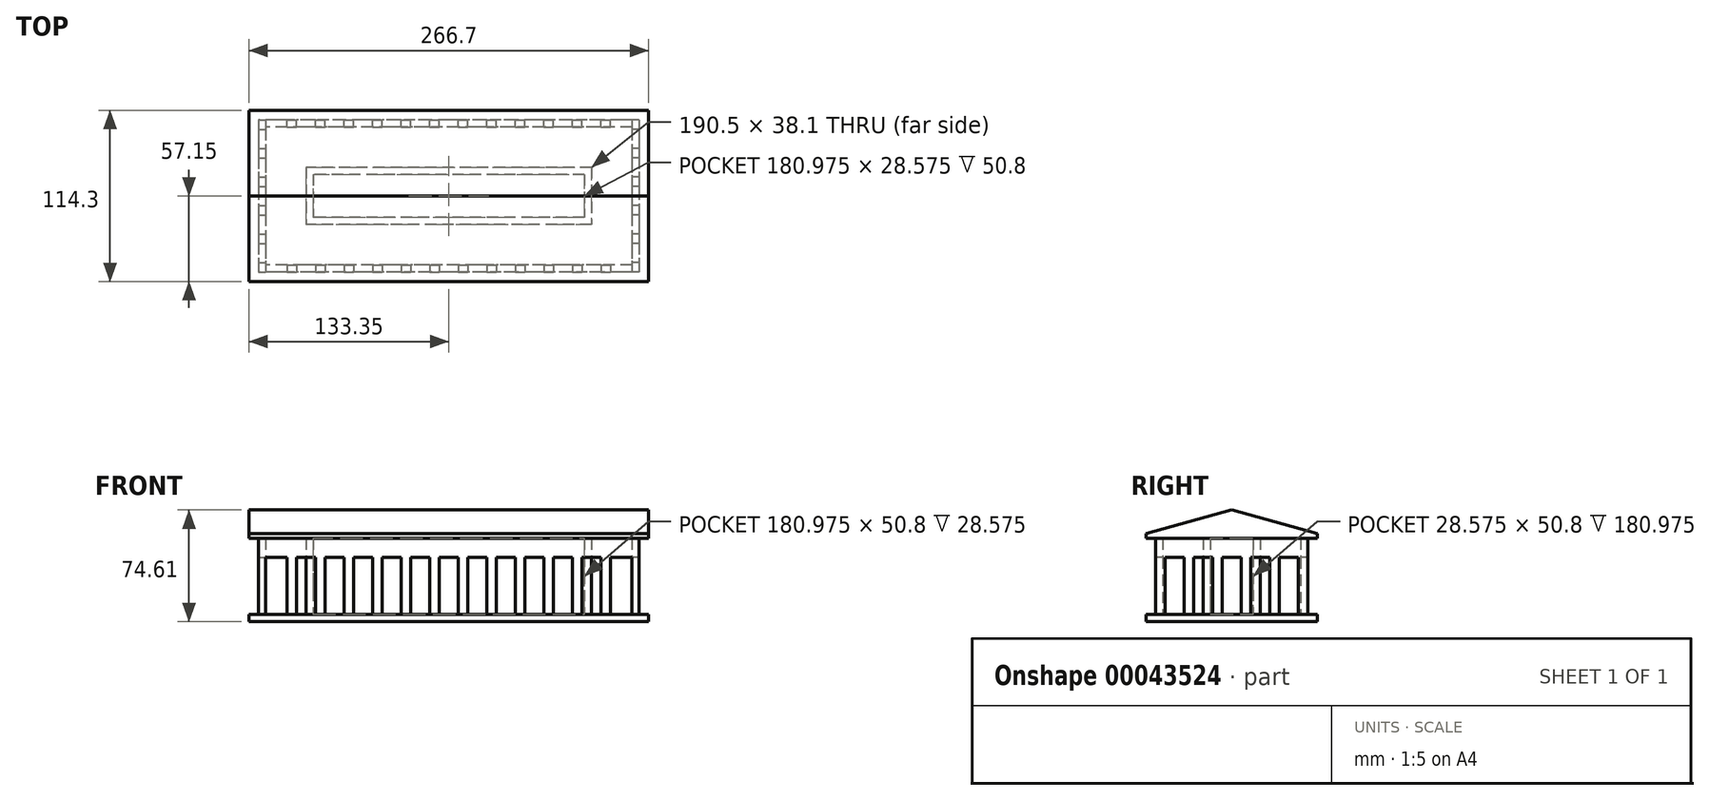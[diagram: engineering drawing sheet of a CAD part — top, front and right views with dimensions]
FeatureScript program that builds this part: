
annotation { "Feature Type Name" : "Feature", "Feature Type Description" : "" }
export const myFeature = defineFeature(function(context is Context, id is Id, definition is map)
    precondition{}
    {
        {
            var Q0;
            Q0=qCreatedBy(makeId("Top.planeOp"),FACE);
            var sketch = newSketch(context, id + "F0", { "sketchPlane" : qUnion([Q0])});
            skLineSegment(sketch, "E0.bottom", {"start": v(0, 0) * mm, "end": v(-266.7, 0) * mm});
            skLineSegment(sketch, "E0.top", {"start": v(0, -114.3) * mm, "end": v(-266.7, -114.3) * mm});
            skLineSegment(sketch, "E0.left", {"start": v(0, 0) * mm, "end": v(0, -114.3) * mm});
            skLineSegment(sketch, "E0.right", {"start": v(-266.7, 0) * mm, "end": v(-266.7, -114.3) * mm});
            skSolve(sketch);
        }
        {
            var Q0;
            Q0 = qSketchRegion(id + "F0", true);
            var Q1;
            Q1 = qSketchRegion(id + "FEWzJ1hWetXT4Pq_1", true);
            extrude(context, id + "F1", {"entities" : qUnion([Q0, Q1]), "depth" : 4.78 * mm});
        }
        {
            var Q0;
            Q0=makeQuery(id+"F1.opExtrude","CAP_FACE",FACE,{"disambiguationData":[OSD([sQuery(id+"F0.wireOp",EDGE,"E0.bottom"),sQuery(id+"F0.wireOp",EDGE,"E0.top"),sQuery(id+"F0.wireOp",EDGE,"E0.left"),sQuery(id+"F0.wireOp",EDGE,"E0.right")])],"isStart":false});
            var sketch = newSketch(context, id + "F2", { "sketchPlane" : qUnion([Q0])});
            skLineSegment(sketch, "E1.bottom", {"start": v(-260.35, -101.6) * mm, "end": v(-255.59, -101.6) * mm});
            skLineSegment(sketch, "E1.top", {"start": v(-260.35, -107.95) * mm, "end": v(-255.59, -107.95) * mm});
            skLineSegment(sketch, "E1.left", {"start": v(-260.35, -101.6) * mm, "end": v(-260.35, -107.95) * mm});
            skLineSegment(sketch, "E1.right", {"start": v(-255.59, -101.6) * mm, "end": v(-255.59, -107.95) * mm});
            skLineSegment(sketch, "E2.0.1.0", {"start": v(-260.35, -88.9) * mm, "end": v(-255.59, -88.9) * mm});
            skLineSegment(sketch, "E2.0.1.1", {"start": v(-255.59, -82.55) * mm, "end": v(-255.59, -88.9) * mm});
            skLineSegment(sketch, "E2.0.1.2", {"start": v(-260.35, -82.55) * mm, "end": v(-260.35, -88.9) * mm});
            skLineSegment(sketch, "E2.0.1.3", {"start": v(-260.35, -82.55) * mm, "end": v(-255.59, -82.55) * mm});
            skLineSegment(sketch, "E2.0.2.0", {"start": v(-260.35, -69.85) * mm, "end": v(-255.59, -69.85) * mm});
            skLineSegment(sketch, "E2.0.2.1", {"start": v(-255.59, -63.5) * mm, "end": v(-255.59, -69.85) * mm});
            skLineSegment(sketch, "E2.0.2.2", {"start": v(-260.35, -63.5) * mm, "end": v(-260.35, -69.85) * mm});
            skLineSegment(sketch, "E2.0.2.3", {"start": v(-260.35, -63.5) * mm, "end": v(-255.59, -63.5) * mm});
            skLineSegment(sketch, "E2.0.3.0", {"start": v(-260.35, -50.8) * mm, "end": v(-255.59, -50.8) * mm});
            skLineSegment(sketch, "E2.0.3.1", {"start": v(-255.59, -44.45) * mm, "end": v(-255.59, -50.8) * mm});
            skLineSegment(sketch, "E2.0.3.2", {"start": v(-260.35, -44.45) * mm, "end": v(-260.35, -50.8) * mm});
            skLineSegment(sketch, "E2.0.3.3", {"start": v(-260.35, -44.45) * mm, "end": v(-255.59, -44.45) * mm});
            skLineSegment(sketch, "E2.0.4.0", {"start": v(-260.35, -31.75) * mm, "end": v(-255.59, -31.75) * mm});
            skLineSegment(sketch, "E2.0.4.1", {"start": v(-255.59, -25.4) * mm, "end": v(-255.59, -31.75) * mm});
            skLineSegment(sketch, "E2.0.4.2", {"start": v(-260.35, -25.4) * mm, "end": v(-260.35, -31.75) * mm});
            skLineSegment(sketch, "E2.0.4.3", {"start": v(-260.35, -25.4) * mm, "end": v(-255.59, -25.4) * mm});
            skLineSegment(sketch, "E2.0.5.0", {"start": v(-260.35, -12.7) * mm, "end": v(-255.59, -12.7) * mm});
            skLineSegment(sketch, "E2.0.5.1", {"start": v(-255.59, -6.35) * mm, "end": v(-255.59, -12.7) * mm});
            skLineSegment(sketch, "E2.0.5.2", {"start": v(-260.35, -6.35) * mm, "end": v(-260.35, -12.7) * mm});
            skLineSegment(sketch, "E2.0.5.3", {"start": v(-260.35, -6.35) * mm, "end": v(-255.59, -6.35) * mm});
            skLineSegment(sketch, "E2.direction1", {"start": v(-260.35, -107.95) * mm, "end": v(-251.94, -107.95) * mm, "construction": true});
            skLineSegment(sketch, "E2.direction2", {"start": v(-260.35, -107.95) * mm, "end": v(-260.35, -88.9) * mm, "construction": true});
            skLineSegment(sketch, "E3.bottom", {"start": v(-241.3, -103.19) * mm, "end": v(-234.95, -103.19) * mm});
            skLineSegment(sketch, "E3.top", {"start": v(-241.3, -107.95) * mm, "end": v(-234.95, -107.95) * mm});
            skLineSegment(sketch, "E3.left", {"start": v(-241.3, -103.19) * mm, "end": v(-241.3, -107.95) * mm});
            skLineSegment(sketch, "E3.right", {"start": v(-234.95, -103.19) * mm, "end": v(-234.95, -107.95) * mm});
            skLineSegment(sketch, "E4.1.0.0", {"start": v(-222.25, -107.95) * mm, "end": v(-215.9, -107.95) * mm});
            skLineSegment(sketch, "E4.1.0.1", {"start": v(-215.9, -103.19) * mm, "end": v(-215.9, -107.95) * mm});
            skLineSegment(sketch, "E4.1.0.2", {"start": v(-222.25, -103.19) * mm, "end": v(-222.25, -107.95) * mm});
            skLineSegment(sketch, "E4.1.0.3", {"start": v(-222.25, -103.19) * mm, "end": v(-215.9, -103.19) * mm});
            skLineSegment(sketch, "E4.2.0.0", {"start": v(-203.2, -107.95) * mm, "end": v(-196.85, -107.95) * mm});
            skLineSegment(sketch, "E4.2.0.1", {"start": v(-196.85, -103.19) * mm, "end": v(-196.85, -107.95) * mm});
            skLineSegment(sketch, "E4.2.0.2", {"start": v(-203.2, -103.19) * mm, "end": v(-203.2, -107.95) * mm});
            skLineSegment(sketch, "E4.2.0.3", {"start": v(-203.2, -103.19) * mm, "end": v(-196.85, -103.19) * mm});
            skLineSegment(sketch, "E4.3.0.0", {"start": v(-184.15, -107.95) * mm, "end": v(-177.8, -107.95) * mm});
            skLineSegment(sketch, "E4.3.0.1", {"start": v(-177.8, -103.19) * mm, "end": v(-177.8, -107.95) * mm});
            skLineSegment(sketch, "E4.3.0.2", {"start": v(-184.15, -103.19) * mm, "end": v(-184.15, -107.95) * mm});
            skLineSegment(sketch, "E4.3.0.3", {"start": v(-184.15, -103.19) * mm, "end": v(-177.8, -103.19) * mm});
            skLineSegment(sketch, "E4.4.0.0", {"start": v(-165.1, -107.95) * mm, "end": v(-158.75, -107.95) * mm});
            skLineSegment(sketch, "E4.4.0.1", {"start": v(-158.75, -103.19) * mm, "end": v(-158.75, -107.95) * mm});
            skLineSegment(sketch, "E4.4.0.2", {"start": v(-165.1, -103.19) * mm, "end": v(-165.1, -107.95) * mm});
            skLineSegment(sketch, "E4.4.0.3", {"start": v(-165.1, -103.19) * mm, "end": v(-158.75, -103.19) * mm});
            skLineSegment(sketch, "E4.5.0.0", {"start": v(-146.05, -107.95) * mm, "end": v(-139.7, -107.95) * mm});
            skLineSegment(sketch, "E4.5.0.1", {"start": v(-139.7, -103.19) * mm, "end": v(-139.7, -107.95) * mm});
            skLineSegment(sketch, "E4.5.0.2", {"start": v(-146.05, -103.19) * mm, "end": v(-146.05, -107.95) * mm});
            skLineSegment(sketch, "E4.5.0.3", {"start": v(-146.05, -103.19) * mm, "end": v(-139.7, -103.19) * mm});
            skLineSegment(sketch, "E4.6.0.0", {"start": v(-127, -107.95) * mm, "end": v(-120.65, -107.95) * mm});
            skLineSegment(sketch, "E4.6.0.1", {"start": v(-120.65, -103.19) * mm, "end": v(-120.65, -107.95) * mm});
            skLineSegment(sketch, "E4.6.0.2", {"start": v(-127, -103.19) * mm, "end": v(-127, -107.95) * mm});
            skLineSegment(sketch, "E4.6.0.3", {"start": v(-127, -103.19) * mm, "end": v(-120.65, -103.19) * mm});
            skLineSegment(sketch, "E4.7.0.0", {"start": v(-107.95, -107.95) * mm, "end": v(-101.6, -107.95) * mm});
            skLineSegment(sketch, "E4.7.0.1", {"start": v(-101.6, -103.19) * mm, "end": v(-101.6, -107.95) * mm});
            skLineSegment(sketch, "E4.7.0.2", {"start": v(-107.95, -103.19) * mm, "end": v(-107.95, -107.95) * mm});
            skLineSegment(sketch, "E4.7.0.3", {"start": v(-107.95, -103.19) * mm, "end": v(-101.6, -103.19) * mm});
            skLineSegment(sketch, "E4.8.0.0", {"start": v(-88.9, -107.95) * mm, "end": v(-82.55, -107.95) * mm});
            skLineSegment(sketch, "E4.8.0.1", {"start": v(-82.55, -103.19) * mm, "end": v(-82.55, -107.95) * mm});
            skLineSegment(sketch, "E4.8.0.2", {"start": v(-88.9, -103.19) * mm, "end": v(-88.9, -107.95) * mm});
            skLineSegment(sketch, "E4.8.0.3", {"start": v(-88.9, -103.19) * mm, "end": v(-82.55, -103.19) * mm});
            skLineSegment(sketch, "E4.9.0.0", {"start": v(-69.85, -107.95) * mm, "end": v(-63.5, -107.95) * mm});
            skLineSegment(sketch, "E4.9.0.1", {"start": v(-63.5, -103.19) * mm, "end": v(-63.5, -107.95) * mm});
            skLineSegment(sketch, "E4.9.0.2", {"start": v(-69.85, -103.19) * mm, "end": v(-69.85, -107.95) * mm});
            skLineSegment(sketch, "E4.9.0.3", {"start": v(-69.85, -103.19) * mm, "end": v(-63.5, -103.19) * mm});
            skLineSegment(sketch, "E4.10.0.0", {"start": v(-50.8, -107.95) * mm, "end": v(-44.45, -107.95) * mm});
            skLineSegment(sketch, "E4.10.0.1", {"start": v(-44.45, -103.19) * mm, "end": v(-44.45, -107.95) * mm});
            skLineSegment(sketch, "E4.10.0.2", {"start": v(-50.8, -103.19) * mm, "end": v(-50.8, -107.95) * mm});
            skLineSegment(sketch, "E4.10.0.3", {"start": v(-50.8, -103.19) * mm, "end": v(-44.45, -103.19) * mm});
            skLineSegment(sketch, "E4.11.0.0", {"start": v(-31.75, -107.95) * mm, "end": v(-25.4, -107.95) * mm});
            skLineSegment(sketch, "E4.11.0.1", {"start": v(-25.4, -103.19) * mm, "end": v(-25.4, -107.95) * mm});
            skLineSegment(sketch, "E4.11.0.2", {"start": v(-31.75, -103.19) * mm, "end": v(-31.75, -107.95) * mm});
            skLineSegment(sketch, "E4.11.0.3", {"start": v(-31.75, -103.19) * mm, "end": v(-25.4, -103.19) * mm});
            skLineSegment(sketch, "E4.direction1", {"start": v(-241.3, -107.95) * mm, "end": v(-222.25, -107.95) * mm, "construction": true});
            skLineSegment(sketch, "E5.MirrorCS", {"start": v(-6.35, -107.95) * mm, "end": v(-11.11, -107.95) * mm});
            skLineSegment(sketch, "E6.MirrorCS", {"start": v(-6.35, -82.55) * mm, "end": v(-6.35, -88.9) * mm});
            skLineSegment(sketch, "E7.MirrorCS", {"start": v(-6.35, -82.55) * mm, "end": v(-11.11, -82.55) * mm});
            skLineSegment(sketch, "E8.MirrorCS", {"start": v(-6.35, -12.7) * mm, "end": v(-11.11, -12.7) * mm});
            skLineSegment(sketch, "E9.MirrorCS", {"start": v(-11.11, -6.35) * mm, "end": v(-11.11, -12.7) * mm});
            skLineSegment(sketch, "E10.MirrorCS", {"start": v(-6.35, -6.35) * mm, "end": v(-6.35, -12.7) * mm});
            skLineSegment(sketch, "E11.MirrorCS", {"start": v(-6.35, -6.35) * mm, "end": v(-11.11, -6.35) * mm});
            skLineSegment(sketch, "E12.MirrorCS", {"start": v(-6.35, -31.75) * mm, "end": v(-11.11, -31.75) * mm});
            skLineSegment(sketch, "E13.MirrorCS", {"start": v(-11.11, -25.4) * mm, "end": v(-11.11, -31.75) * mm});
            skLineSegment(sketch, "E14.MirrorCS", {"start": v(-11.11, -44.45) * mm, "end": v(-11.11, -50.8) * mm});
            skLineSegment(sketch, "E15.MirrorCS", {"start": v(-6.35, -44.45) * mm, "end": v(-6.35, -50.8) * mm});
            skLineSegment(sketch, "E16.MirrorCS", {"start": v(-6.35, -44.45) * mm, "end": v(-11.11, -44.45) * mm});
            skLineSegment(sketch, "E17.MirrorCS", {"start": v(-6.35, -25.4) * mm, "end": v(-6.35, -31.75) * mm});
            skLineSegment(sketch, "E18.MirrorCS", {"start": v(-11.11, -63.5) * mm, "end": v(-11.11, -69.85) * mm});
            skLineSegment(sketch, "E19.MirrorCS", {"start": v(-6.35, -101.6) * mm, "end": v(-11.11, -101.6) * mm});
            skLineSegment(sketch, "E20.MirrorCS", {"start": v(-6.35, -101.6) * mm, "end": v(-6.35, -107.95) * mm});
            skLineSegment(sketch, "E21.MirrorCS", {"start": v(-6.35, -63.5) * mm, "end": v(-6.35, -69.85) * mm});
            skLineSegment(sketch, "E22.MirrorCS", {"start": v(-6.35, -69.85) * mm, "end": v(-11.11, -69.85) * mm});
            skLineSegment(sketch, "E23.MirrorCS", {"start": v(-11.11, -101.6) * mm, "end": v(-11.11, -107.95) * mm});
            skLineSegment(sketch, "E24.MirrorCS", {"start": v(-6.35, -88.9) * mm, "end": v(-11.11, -88.9) * mm});
            skLineSegment(sketch, "E25.MirrorCS", {"start": v(-6.35, -63.5) * mm, "end": v(-11.11, -63.5) * mm});
            skLineSegment(sketch, "E26.MirrorCS", {"start": v(-6.35, -50.8) * mm, "end": v(-11.11, -50.8) * mm});
            skLineSegment(sketch, "E27.MirrorCS", {"start": v(-11.11, -82.55) * mm, "end": v(-11.11, -88.9) * mm});
            skLineSegment(sketch, "E28.MirrorCS", {"start": v(-6.35, -25.4) * mm, "end": v(-11.11, -25.4) * mm});
            skLineSegment(sketch, "E29.direction1", {"start": v(0, 0) * mm, "end": v(25.4, 0) * mm, "construction": true});
            skLineSegment(sketch, "E30.MirrorCS", {"start": v(-120.65, -11.11) * mm, "end": v(-120.65, -6.35) * mm});
            skLineSegment(sketch, "E31.MirrorCS", {"start": v(-203.2, -6.35) * mm, "end": v(-196.85, -6.35) * mm});
            skLineSegment(sketch, "E32.MirrorCS", {"start": v(-184.15, -11.11) * mm, "end": v(-177.8, -11.11) * mm});
            skLineSegment(sketch, "E33.MirrorCS", {"start": v(-31.75, -11.11) * mm, "end": v(-25.4, -11.11) * mm});
            skLineSegment(sketch, "E34.MirrorCS", {"start": v(-203.2, -11.11) * mm, "end": v(-203.2, -6.35) * mm});
            skLineSegment(sketch, "E35.MirrorCS", {"start": v(-177.8, -11.11) * mm, "end": v(-177.8, -6.35) * mm});
            skLineSegment(sketch, "E36.MirrorCS", {"start": v(-196.85, -11.11) * mm, "end": v(-196.85, -6.35) * mm});
            skLineSegment(sketch, "E37.MirrorCS", {"start": v(-165.1, -6.35) * mm, "end": v(-158.75, -6.35) * mm});
            skLineSegment(sketch, "E38.MirrorCS", {"start": v(-25.4, -11.11) * mm, "end": v(-25.4, -6.35) * mm});
            skLineSegment(sketch, "E39.MirrorCS", {"start": v(-241.3, -11.11) * mm, "end": v(-234.95, -11.11) * mm});
            skLineSegment(sketch, "E40.MirrorCS", {"start": v(-88.9, -6.35) * mm, "end": v(-82.55, -6.35) * mm});
            skLineSegment(sketch, "E41.MirrorCS", {"start": v(-165.1, -11.11) * mm, "end": v(-158.75, -11.11) * mm});
            skLineSegment(sketch, "E42.MirrorCS", {"start": v(-146.05, -11.11) * mm, "end": v(-146.05, -6.35) * mm});
            skLineSegment(sketch, "E43.MirrorCS", {"start": v(-69.85, -11.11) * mm, "end": v(-69.85, -6.35) * mm});
            skLineSegment(sketch, "E44.MirrorCS", {"start": v(-88.9, -11.11) * mm, "end": v(-88.9, -6.35) * mm});
            skLineSegment(sketch, "E45.MirrorCS", {"start": v(-234.95, -11.11) * mm, "end": v(-234.95, -6.35) * mm});
            skLineSegment(sketch, "E46.MirrorCS", {"start": v(-165.1, -11.11) * mm, "end": v(-165.1, -6.35) * mm});
            skLineSegment(sketch, "E47.MirrorCS", {"start": v(-241.3, -11.11) * mm, "end": v(-241.3, -6.35) * mm});
            skLineSegment(sketch, "E48.MirrorCS", {"start": v(-222.25, -6.35) * mm, "end": v(-215.9, -6.35) * mm});
            skLineSegment(sketch, "E49.MirrorCS", {"start": v(-203.2, -11.11) * mm, "end": v(-196.85, -11.11) * mm});
            skLineSegment(sketch, "E50.MirrorCS", {"start": v(-146.05, -11.11) * mm, "end": v(-139.7, -11.11) * mm});
            skLineSegment(sketch, "E51.MirrorCS", {"start": v(-107.95, -6.35) * mm, "end": v(-101.6, -6.35) * mm});
            skLineSegment(sketch, "E52.MirrorCS", {"start": v(-63.5, -11.11) * mm, "end": v(-63.5, -6.35) * mm});
            skLineSegment(sketch, "E53.MirrorCS", {"start": v(-127, -6.35) * mm, "end": v(-120.65, -6.35) * mm});
            skLineSegment(sketch, "E54.MirrorCS", {"start": v(-69.85, -11.11) * mm, "end": v(-63.5, -11.11) * mm});
            skLineSegment(sketch, "E55.MirrorCS", {"start": v(-50.8, -6.35) * mm, "end": v(-44.45, -6.35) * mm});
            skLineSegment(sketch, "E56.MirrorCS", {"start": v(-184.15, -11.11) * mm, "end": v(-184.15, -6.35) * mm});
            skLineSegment(sketch, "E57.MirrorCS", {"start": v(-107.95, -11.11) * mm, "end": v(-101.6, -11.11) * mm});
            skLineSegment(sketch, "E58.MirrorCS", {"start": v(-241.3, -6.35) * mm, "end": v(-234.95, -6.35) * mm});
            skLineSegment(sketch, "E59.MirrorCS", {"start": v(-50.8, -11.11) * mm, "end": v(-50.8, -6.35) * mm});
            skLineSegment(sketch, "E60.MirrorCS", {"start": v(-107.95, -11.11) * mm, "end": v(-107.95, -6.35) * mm});
            skLineSegment(sketch, "E61.MirrorCS", {"start": v(-44.45, -11.11) * mm, "end": v(-44.45, -6.35) * mm});
            skLineSegment(sketch, "E62.MirrorCS", {"start": v(-222.25, -11.11) * mm, "end": v(-222.25, -6.35) * mm});
            skLineSegment(sketch, "E63.MirrorCS", {"start": v(-82.55, -11.11) * mm, "end": v(-82.55, -6.35) * mm});
            skLineSegment(sketch, "E64.MirrorCS", {"start": v(-101.6, -11.11) * mm, "end": v(-101.6, -6.35) * mm});
            skLineSegment(sketch, "E65.MirrorCS", {"start": v(-31.75, -11.11) * mm, "end": v(-31.75, -6.35) * mm});
            skLineSegment(sketch, "E66.MirrorCS", {"start": v(-88.9, -11.11) * mm, "end": v(-82.55, -11.11) * mm});
            skLineSegment(sketch, "E67.MirrorCS", {"start": v(-139.7, -11.11) * mm, "end": v(-139.7, -6.35) * mm});
            skLineSegment(sketch, "E68.MirrorCS", {"start": v(-31.75, -6.35) * mm, "end": v(-25.4, -6.35) * mm});
            skLineSegment(sketch, "E69.MirrorCS", {"start": v(-50.8, -11.11) * mm, "end": v(-44.45, -11.11) * mm});
            skLineSegment(sketch, "E70.MirrorCS", {"start": v(-69.85, -6.35) * mm, "end": v(-63.5, -6.35) * mm});
            skLineSegment(sketch, "E71.MirrorCS", {"start": v(-127, -11.11) * mm, "end": v(-120.65, -11.11) * mm});
            skLineSegment(sketch, "E72.MirrorCS", {"start": v(-127, -11.11) * mm, "end": v(-127, -6.35) * mm});
            skLineSegment(sketch, "E73.MirrorCS", {"start": v(-222.25, -11.11) * mm, "end": v(-215.9, -11.11) * mm});
            skLineSegment(sketch, "E74.MirrorCS", {"start": v(-215.9, -11.11) * mm, "end": v(-215.9, -6.35) * mm});
            skLineSegment(sketch, "E75.MirrorCS", {"start": v(-146.05, -6.35) * mm, "end": v(-139.7, -6.35) * mm});
            skLineSegment(sketch, "E76.MirrorCS", {"start": v(-158.75, -11.11) * mm, "end": v(-158.75, -6.35) * mm});
            skLineSegment(sketch, "E77.MirrorCS", {"start": v(-184.15, -6.35) * mm, "end": v(-177.8, -6.35) * mm});
            skSolve(sketch);
        }
        {
            var Q0;
            Q0 = qSketchRegion(id + "F2", true);
            var Q1;
            Q1 = qSketchRegion(id + "F6IGndgWyHRMqrs_1", true);
            extrude(context, id + "F3", {"entities" : qUnion([Q0, Q1]), "operationType" : NewBodyOperationType.ADD, "depth" : 38.1 * mm});
        }
        {
            var Q0;
            Q0=makeQuery(id+"F1.opExtrude","CAP_FACE",FACE,{"disambiguationData":[OSD([sQuery(id+"F0.wireOp",EDGE,"E0.bottom"),sQuery(id+"F0.wireOp",EDGE,"E0.top"),sQuery(id+"F0.wireOp",EDGE,"E0.left"),sQuery(id+"F0.wireOp",EDGE,"E0.right")])],"isStart":false});
            var sketch = newSketch(context, id + "F4", { "sketchPlane" : qUnion([Q0])});
            skLineSegment(sketch, "E78.0", {"start": v(-38.1, -38.1) * mm, "end": v(-228.6, -38.1) * mm});
            skLineSegment(sketch, "E78.1", {"start": v(-38.1, -38.1) * mm, "end": v(-38.1, -76.2) * mm});
            skLineSegment(sketch, "E78.2", {"start": v(-38.1, -76.2) * mm, "end": v(-228.6, -76.2) * mm});
            skLineSegment(sketch, "E78.3", {"start": v(-228.6, -38.1) * mm, "end": v(-228.6, -76.2) * mm});
            skLineSegment(sketch, "E79.0", {"start": v(-42.86, -42.86) * mm, "end": v(-223.84, -42.86) * mm});
            skLineSegment(sketch, "E79.1", {"start": v(-42.86, -42.86) * mm, "end": v(-42.86, -71.44) * mm});
            skLineSegment(sketch, "E79.2", {"start": v(-42.86, -71.44) * mm, "end": v(-223.84, -71.44) * mm});
            skLineSegment(sketch, "E79.3", {"start": v(-223.84, -42.86) * mm, "end": v(-223.84, -71.44) * mm});
            skLineSegment(sketch, "E80.0", {"start": v(-6.35, -107.95) * mm, "end": v(-6.35, -6.35) * mm});
            skLineSegment(sketch, "E80.1", {"start": v(-260.35, -107.95) * mm, "end": v(-6.35, -107.95) * mm});
            skLineSegment(sketch, "E80.2", {"start": v(-260.35, -6.35) * mm, "end": v(-260.35, -107.95) * mm});
            skLineSegment(sketch, "E80.3", {"start": v(-6.35, -6.35) * mm, "end": v(-260.35, -6.35) * mm});
            skLineSegment(sketch, "E81.0", {"start": v(0, -107.95) * mm, "end": v(0, -6.35) * mm});
            skSolve(sketch);
        }
        {
            var Q0;
            Q0=makeQuery(id+"F4.imprint","IMPRINT",FACE,{"disambiguationData":[TD([[makeQuery(id+"F4.imprint","IMPRINT",EDGE,{"derivedFrom":sQuery(id+"F4.wireOp",EDGE,"E78.0")}),1.0]])]});
            extrude(context, id + "F5", {"entities" : qUnion([Q0]), "operationType" : NewBodyOperationType.ADD, "depth" : 50.8 * mm});
        }
        {
            var Q0;
            Q0=makeQuery(id+"F3.opExtrude","CAP_FACE",FACE,{"disambiguationData":[OSD([sQuery(id+"F2.wireOp",EDGE,"E48.MirrorCS"),sQuery(id+"F2.wireOp",EDGE,"E62.MirrorCS"),sQuery(id+"F2.wireOp",EDGE,"E73.MirrorCS"),sQuery(id+"F2.wireOp",EDGE,"E74.MirrorCS")])],"isStart":false});
            var sketch = newSketch(context, id + "F6", { "sketchPlane" : qUnion([Q0])});
            skLineSegment(sketch, "E82.bottom", {"start": v(-6.35, -6.35) * mm, "end": v(-260.35, -6.35) * mm});
            skLineSegment(sketch, "E82.top", {"start": v(-6.35, -107.95) * mm, "end": v(-260.35, -107.95) * mm});
            skLineSegment(sketch, "E82.left", {"start": v(-6.35, -6.35) * mm, "end": v(-6.35, -107.95) * mm});
            skLineSegment(sketch, "E82.right", {"start": v(-260.35, -6.35) * mm, "end": v(-260.35, -107.95) * mm});
            skLineSegment(sketch, "E83.0", {"start": v(-11.11, -11.11) * mm, "end": v(-255.59, -11.11) * mm});
            skLineSegment(sketch, "E83.1", {"start": v(-11.11, -11.11) * mm, "end": v(-11.11, -103.19) * mm});
            skLineSegment(sketch, "E83.2", {"start": v(-11.11, -103.19) * mm, "end": v(-255.59, -103.19) * mm});
            skLineSegment(sketch, "E83.3", {"start": v(-255.59, -11.11) * mm, "end": v(-255.59, -103.19) * mm});
            skLineSegment(sketch, "E84.0", {"start": v(-6.35, -107.95) * mm, "end": v(-6.35, -6.35) * mm});
            skLineSegment(sketch, "E84.1", {"start": v(-260.35, -107.95) * mm, "end": v(-6.35, -107.95) * mm});
            skSolve(sketch);
        }
        {
            var Q0;
            Q0 = qSketchRegion(id + "F6", true);
            extrude(context, id + "F7", {"entities" : qUnion([Q0]), "operationType" : NewBodyOperationType.ADD, "depth" : 12.7 * mm});
        }
        {
            var Q0;
            Q0=makeQuery(id+"F1.opExtrude","SWEPT_FACE",FACE,{"disambiguationData":[OSD([sQuery(id+"F0.wireOp",EDGE,"E0.right")])]});
            var sketch = newSketch(context, id + "F8", { "sketchPlane" : qUnion([Q0])});
            skLineSegment(sketch, "E85.0.0", {"start": v(101.6, 4.78) * mm, "end": v(107.95, 4.78) * mm});
            skLineSegment(sketch, "E85.0.1", {"start": v(107.95, 4.78) * mm, "end": v(107.95, 55.58) * mm});
            skLineSegment(sketch, "E85.0.2", {"start": v(107.95, 55.58) * mm, "end": v(6.35, 55.58) * mm});
            skLineSegment(sketch, "E85.0.3", {"start": v(6.35, 55.58) * mm, "end": v(6.35, 4.78) * mm});
            skLineSegment(sketch, "E85.0.4", {"start": v(6.35, 4.78) * mm, "end": v(12.7, 4.78) * mm});
            skLineSegment(sketch, "E85.0.5", {"start": v(12.7, 4.78) * mm, "end": v(12.7, 42.88) * mm});
            skLineSegment(sketch, "E85.0.6", {"start": v(12.7, 42.88) * mm, "end": v(25.4, 42.88) * mm});
            skLineSegment(sketch, "E85.0.7", {"start": v(25.4, 42.88) * mm, "end": v(25.4, 4.78) * mm});
            skLineSegment(sketch, "E85.0.8", {"start": v(25.4, 4.78) * mm, "end": v(31.75, 4.78) * mm});
            skLineSegment(sketch, "E85.0.9", {"start": v(31.75, 4.78) * mm, "end": v(31.75, 42.88) * mm});
            skLineSegment(sketch, "E85.0.10", {"start": v(31.75, 42.88) * mm, "end": v(44.45, 42.88) * mm});
            skLineSegment(sketch, "E85.0.11", {"start": v(44.45, 42.88) * mm, "end": v(44.45, 4.78) * mm});
            skLineSegment(sketch, "E85.0.12", {"start": v(44.45, 4.78) * mm, "end": v(50.8, 4.78) * mm});
            skLineSegment(sketch, "E85.0.13", {"start": v(50.8, 4.78) * mm, "end": v(50.8, 42.88) * mm});
            skLineSegment(sketch, "E85.0.14", {"start": v(50.8, 42.88) * mm, "end": v(63.5, 42.88) * mm});
            skLineSegment(sketch, "E85.0.15", {"start": v(63.5, 42.88) * mm, "end": v(63.5, 4.78) * mm});
            skLineSegment(sketch, "E85.0.16", {"start": v(63.5, 4.78) * mm, "end": v(69.85, 4.78) * mm});
            skLineSegment(sketch, "E85.0.17", {"start": v(69.85, 4.78) * mm, "end": v(69.85, 42.88) * mm});
            skLineSegment(sketch, "E85.0.18", {"start": v(69.85, 42.88) * mm, "end": v(82.55, 42.88) * mm});
            skLineSegment(sketch, "E85.0.19", {"start": v(82.55, 42.88) * mm, "end": v(82.55, 4.78) * mm});
            skLineSegment(sketch, "E85.0.20", {"start": v(82.55, 4.78) * mm, "end": v(88.9, 4.78) * mm});
            skLineSegment(sketch, "E85.0.21", {"start": v(88.9, 4.78) * mm, "end": v(88.9, 42.88) * mm});
            skLineSegment(sketch, "E85.0.22", {"start": v(88.9, 42.88) * mm, "end": v(101.6, 42.88) * mm});
            skLineSegment(sketch, "E85.0.23", {"start": v(101.6, 42.88) * mm, "end": v(101.6, 4.78) * mm});
            skLineSegment(sketch, "E86", {"start": v(0, 55.58) * mm, "end": v(6.35, 55.58) * mm});
            skLineSegment(sketch, "E87", {"start": v(107.95, 55.58) * mm, "end": v(114.3, 55.58) * mm});
            skLineSegment(sketch, "E88", {"start": v(0, 55.58) * mm, "end": v(0, 58.75) * mm});
            skLineSegment(sketch, "E89", {"start": v(0, 58.75) * mm, "end": v(114.3, 58.75) * mm});
            skLineSegment(sketch, "E90", {"start": v(114.3, 58.75) * mm, "end": v(114.3, 55.58) * mm});
            skLineSegment(sketch, "E91", {"start": v(0, 58.75) * mm, "end": v(57.15, 74.61) * mm});
            skLineSegment(sketch, "E92", {"start": v(57.15, 74.61) * mm, "end": v(114.3, 58.75) * mm});
            skSolve(sketch);
        }
        {
            var Q0;
            Q0=makeQuery(id+"F8.imprint","IMPRINT",FACE,{"disambiguationData":[TD([[makeQuery(id+"F8.imprint","IMPRINT",EDGE,{"derivedFrom":sQuery(id+"F8.wireOp",EDGE,"E89")}),1.0]])]});
            var Q1;
            Q1=makeQuery(id+"F8.imprint","IMPRINT",FACE,{"disambiguationData":[TD([[makeQuery(id+"F8.imprint","IMPRINT",EDGE,{"derivedFrom":sQuery(id+"F8.wireOp",EDGE,"E85.0.2")}),-1.0]])]});
            var Q2;
            Q2=makeQuery(id+"F1.opExtrude","SWEPT_FACE",FACE,{"disambiguationData":[OSD([sQuery(id+"F0.wireOp",EDGE,"E0.left")])]});
            extrude(context, id + "F9", {"entities" : qUnion([Q0, Q1]), "operationType" : NewBodyOperationType.ADD, "endBound" : BoundingType.UP_TO_SURFACE, "oppositeDirection" : true, "endBoundEntityFace" : qUnion([Q2]), "depth" : 25.4 * mm});
        }
    });
